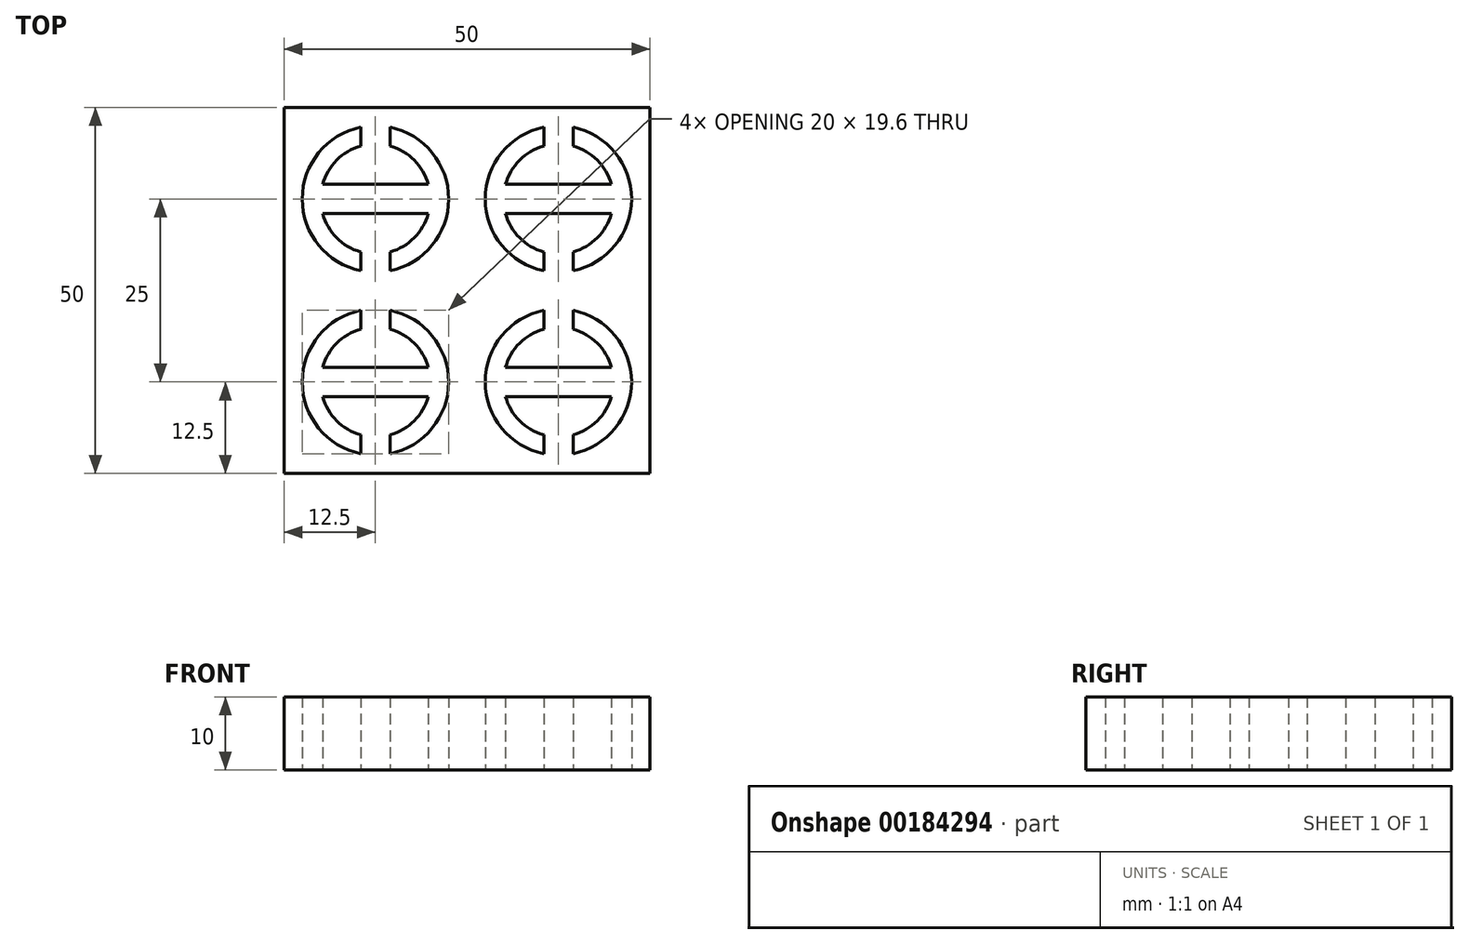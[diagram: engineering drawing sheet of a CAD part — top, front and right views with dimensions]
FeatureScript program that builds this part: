
annotation { "Feature Type Name" : "Feature", "Feature Type Description" : "" }
export const myFeature = defineFeature(function(context is Context, id is Id, definition is map)
    precondition{}
    {
        {
            assignVariable(context, id + "F0", {"name" : "moldThick", "anyValue" : 10});
        }
        {
            var Q0;
            Q0=qCreatedBy(makeId("Top.planeOp"),FACE);
            var sketch = newSketch(context, id + "F1", { "sketchPlane" : qUnion([Q0])});
            skLineSegment(sketch, "E0.rect.bottom", {"start": v(25, 25) * mm, "end": v(-25, 25) * mm});
            skLineSegment(sketch, "E0.rect.top", {"start": v(25, -25) * mm, "end": v(-25, -25) * mm});
            skLineSegment(sketch, "E0.rect.left", {"start": v(25, 25) * mm, "end": v(25, -25) * mm});
            skLineSegment(sketch, "E0.rect.right", {"start": v(-25, 25) * mm, "end": v(-25, -25) * mm});
            skLineSegment(sketch, "E1", {"start": v(0, 25) * mm, "end": v(0, -25) * mm, "construction": true});
            skLineSegment(sketch, "E2", {"start": v(25, 0) * mm, "end": v(-25, 0) * mm, "construction": true});
            skLineSegment(sketch, "E3", {"start": v(-25, 25) * mm, "end": v(0, 0) * mm, "construction": true});
            skLineSegment(sketch, "E4", {"start": v(0, 25) * mm, "end": v(-25, 0) * mm, "construction": true});
            skLineSegment(sketch, "E5.MirrorCS", {"start": v(-25, 0) * mm, "end": v(25, 0) * mm, "construction": true});
            skArc(sketch, "E6", {"start": v(-14.5, 22.3) * mm, "mid": v(-22.5, 12.5) * mm, "end": v(-14.5, 2.7) * mm});
            skArc(sketch, "E7", {"start": v(-19.73, 10.5) * mm, "mid": v(-17.8, 7.2) * mm, "end": v(-14.5, 5.27) * mm});
            skLineSegment(sketch, "E8.rect.bottom", {"start": v(-19.73, 14.5) * mm, "end": v(-5.27, 14.5) * mm});
            skLineSegment(sketch, "E8.rect.top", {"start": v(-19.73, 10.5) * mm, "end": v(-5.27, 10.5) * mm});
            skLineSegment(sketch, "E9", {"start": v(-14.5, 22.3) * mm, "end": v(-14.5, 19.73) * mm});
            skLineSegment(sketch, "E10", {"start": v(-10.5, 2.7) * mm, "end": v(-10.5, 5.27) * mm});
            skLineSegment(sketch, "E11.trimOffspring", {"start": v(-14.5, 5.27) * mm, "end": v(-14.5, 2.7) * mm});
            skLineSegment(sketch, "E12.trimOffspring", {"start": v(-10.5, 19.73) * mm, "end": v(-10.5, 22.3) * mm});
            skArc(sketch, "E13.trimOffspring", {"start": v(-5.27, 14.5) * mm, "mid": v(-7.2, 17.8) * mm, "end": v(-10.5, 19.73) * mm});
            skArc(sketch, "E14.trimOffspring", {"start": v(-10.5, 5.27) * mm, "mid": v(-7.2, 7.2) * mm, "end": v(-5.27, 10.5) * mm});
            skArc(sketch, "E15.trimOffspring", {"start": v(-14.5, 19.73) * mm, "mid": v(-17.8, 17.8) * mm, "end": v(-19.73, 14.5) * mm});
            skPoint(sketch, "E16.orphan", {"position": v(-22.3, 14.5) * mm});
            skPoint(sketch, "E17.orphan", {"position": v(-2.7, 10.5) * mm});
            skArc(sketch, "E18.trimOffspring", {"start": v(-10.5, 2.7) * mm, "mid": v(-2.5, 12.5) * mm, "end": v(-10.5, 22.3) * mm});
            skLineSegment(sketch, "E19.MirrorCS", {"start": v(14.5, 5.27) * mm, "end": v(14.5, 2.7) * mm});
            skLineSegment(sketch, "E20.MirrorCS", {"start": v(14.5, 22.3) * mm, "end": v(14.5, 19.73) * mm});
            skLineSegment(sketch, "E21.MirrorCS", {"start": v(10.5, 2.7) * mm, "end": v(10.5, 5.27) * mm});
            skLineSegment(sketch, "E22.MirrorCS", {"start": v(10.5, 19.73) * mm, "end": v(10.5, 22.3) * mm});
            skPoint(sketch, "E23.MirrorP", {"position": v(12.5, 12.5) * mm});
            skLineSegment(sketch, "E24.MirrorCS", {"start": v(19.73, 14.5) * mm, "end": v(5.27, 14.5) * mm});
            skPoint(sketch, "E25.MirrorP", {"position": v(22.3, 14.5) * mm});
            skArc(sketch, "E26.MirrorCS", {"start": v(19.73, 10.5) * mm, "mid": v(17.8, 7.2) * mm, "end": v(14.5, 5.27) * mm});
            skArc(sketch, "E27.MirrorCS", {"start": v(5.27, 14.5) * mm, "mid": v(7.2, 17.8) * mm, "end": v(10.5, 19.73) * mm});
            skPoint(sketch, "E28.MirrorP", {"position": v(2.7, 10.5) * mm});
            skArc(sketch, "E29.MirrorCS", {"start": v(14.5, 22.3) * mm, "mid": v(22.5, 12.5) * mm, "end": v(14.5, 2.7) * mm});
            skLineSegment(sketch, "E30.MirrorCS", {"start": v(19.73, 10.5) * mm, "end": v(5.27, 10.5) * mm});
            skArc(sketch, "E31.MirrorCS", {"start": v(10.5, 2.7) * mm, "mid": v(2.5, 12.5) * mm, "end": v(10.5, 22.3) * mm});
            skArc(sketch, "E32.MirrorCS", {"start": v(10.5, 5.27) * mm, "mid": v(7.2, 7.2) * mm, "end": v(5.27, 10.5) * mm});
            skArc(sketch, "E33.MirrorCS", {"start": v(14.5, 19.73) * mm, "mid": v(17.8, 17.8) * mm, "end": v(19.73, 14.5) * mm});
            skLineSegment(sketch, "E34.MirrorCS", {"start": v(10.5, -2.7) * mm, "end": v(10.5, -5.27) * mm});
            skLineSegment(sketch, "E35.MirrorCS", {"start": v(-14.5, -22.3) * mm, "end": v(-14.5, -19.73) * mm});
            skLineSegment(sketch, "E36.MirrorCS", {"start": v(-10.5, -19.73) * mm, "end": v(-10.5, -22.3) * mm});
            skLineSegment(sketch, "E37.MirrorCS", {"start": v(14.5, -22.3) * mm, "end": v(14.5, -19.73) * mm});
            skLineSegment(sketch, "E38.MirrorCS", {"start": v(-10.5, -2.7) * mm, "end": v(-10.5, -5.27) * mm});
            skLineSegment(sketch, "E39.MirrorCS", {"start": v(14.5, -5.27) * mm, "end": v(14.5, -2.7) * mm});
            skLineSegment(sketch, "E40.MirrorCS", {"start": v(-14.5, -5.27) * mm, "end": v(-14.5, -2.7) * mm});
            skLineSegment(sketch, "E41.MirrorCS", {"start": v(10.5, -19.73) * mm, "end": v(10.5, -22.3) * mm});
            skPoint(sketch, "E42.MirrorP", {"position": v(12.5, -12.5) * mm});
            skPoint(sketch, "E43.MirrorP", {"position": v(-12.5, -12.5) * mm});
            skArc(sketch, "E44.MirrorCS", {"start": v(19.73, -10.5) * mm, "mid": v(17.8, -7.2) * mm, "end": v(14.5, -5.27) * mm});
            skArc(sketch, "E45.MirrorCS", {"start": v(-14.5, -19.73) * mm, "mid": v(-17.8, -17.8) * mm, "end": v(-19.73, -14.5) * mm});
            skArc(sketch, "E46.MirrorCS", {"start": v(14.5, -19.73) * mm, "mid": v(17.8, -17.8) * mm, "end": v(19.73, -14.5) * mm});
            skArc(sketch, "E47.MirrorCS", {"start": v(-5.27, -14.5) * mm, "mid": v(-7.2, -17.8) * mm, "end": v(-10.5, -19.73) * mm});
            skArc(sketch, "E48.MirrorCS", {"start": v(-10.5, -5.27) * mm, "mid": v(-7.2, -7.2) * mm, "end": v(-5.27, -10.5) * mm});
            skArc(sketch, "E49.MirrorCS", {"start": v(10.5, -2.7) * mm, "mid": v(2.5, -12.5) * mm, "end": v(10.5, -22.3) * mm});
            skPoint(sketch, "E50.MirrorP", {"position": v(-22.3, -14.5) * mm});
            skLineSegment(sketch, "E51.MirrorCS", {"start": v(19.73, -14.5) * mm, "end": v(5.27, -14.5) * mm});
            skArc(sketch, "E52.MirrorCS", {"start": v(14.5, -22.3) * mm, "mid": v(22.5, -12.5) * mm, "end": v(14.5, -2.7) * mm});
            skArc(sketch, "E53.MirrorCS", {"start": v(-10.5, -2.7) * mm, "mid": v(-2.5, -12.5) * mm, "end": v(-10.5, -22.3) * mm});
            skPoint(sketch, "E54.MirrorP", {"position": v(-2.7, -10.5) * mm});
            skPoint(sketch, "E55.MirrorP", {"position": v(2.7, -10.5) * mm});
            skLineSegment(sketch, "E56.MirrorCS", {"start": v(19.73, -10.5) * mm, "end": v(5.27, -10.5) * mm});
            skLineSegment(sketch, "E57.MirrorCS", {"start": v(-19.73, -10.5) * mm, "end": v(-5.27, -10.5) * mm});
            skArc(sketch, "E58.MirrorCS", {"start": v(5.27, -14.5) * mm, "mid": v(7.2, -17.8) * mm, "end": v(10.5, -19.73) * mm});
            skArc(sketch, "E59.MirrorCS", {"start": v(-14.5, -22.3) * mm, "mid": v(-22.5, -12.5) * mm, "end": v(-14.5, -2.7) * mm});
            skArc(sketch, "E60.MirrorCS", {"start": v(10.5, -5.27) * mm, "mid": v(7.2, -7.2) * mm, "end": v(5.27, -10.5) * mm});
            skArc(sketch, "E61.MirrorCS", {"start": v(-19.73, -10.5) * mm, "mid": v(-17.8, -7.2) * mm, "end": v(-14.5, -5.27) * mm});
            skLineSegment(sketch, "E62.MirrorCS", {"start": v(-19.73, -14.5) * mm, "end": v(-5.27, -14.5) * mm});
            skPoint(sketch, "E63.MirrorP", {"position": v(22.3, -14.5) * mm});
            skSolve(sketch);
        }
        {
            var Q0;
            Q0=makeQuery(id+"F1.imprint","IMPRINT",FACE,{"disambiguationData":[TD([[makeQuery(id+"F1.imprint","IMPRINT",EDGE,{"derivedFrom":sQuery(id+"F1.wireOp",EDGE,"E0.rect.bottom")}),1.0]])]});
            extrude(context, id + "F2", {"entities" : qUnion([Q0]), "depth" : (getVariable(context, 'moldThick')) * mm});
        }
    });
